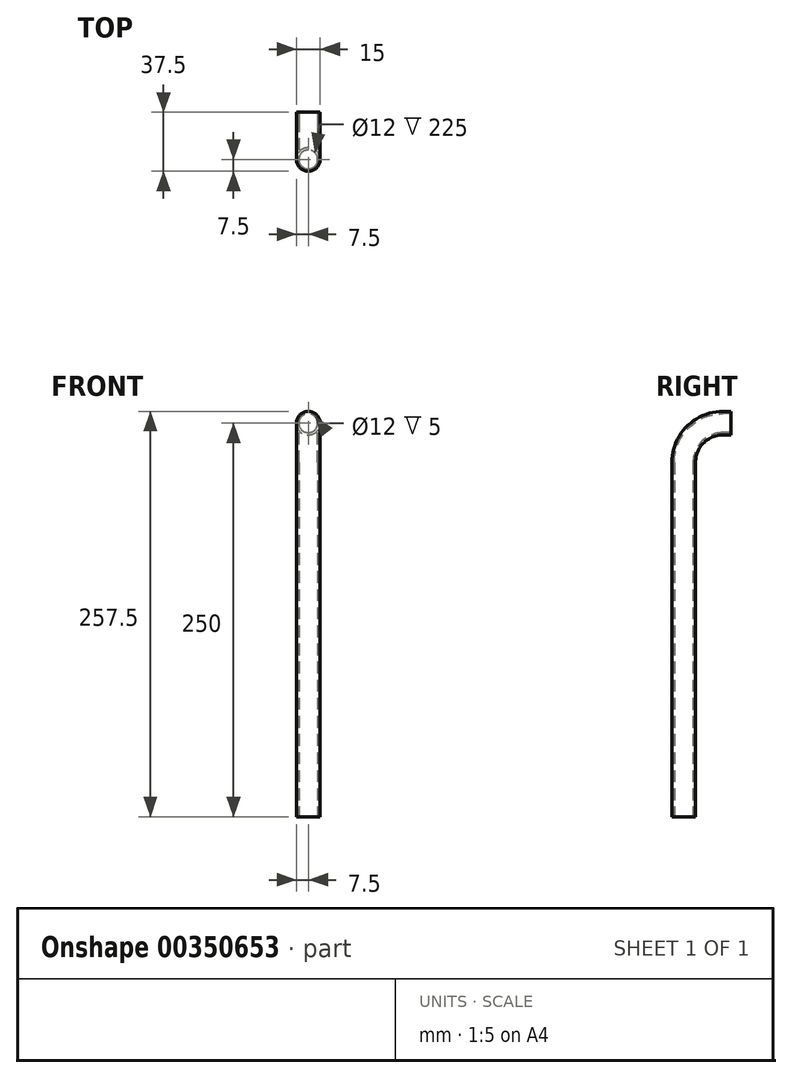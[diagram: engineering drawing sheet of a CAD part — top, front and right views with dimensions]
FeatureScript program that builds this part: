
annotation { "Feature Type Name" : "Feature", "Feature Type Description" : "" }
export const myFeature = defineFeature(function(context is Context, id is Id, definition is map)
    precondition{}
    {
        {
            var Q0;
            Q0=qCreatedBy(makeId("Right.planeOp"),FACE);
            var sketch = newSketch(context, id + "F0", { "sketchPlane" : qUnion([Q0])});
            skLineSegment(sketch, "E0", {"start": v(0, 0) * mm, "end": v(-5, 0) * mm});
            skLineSegment(sketch, "E1", {"start": v(-30, -25) * mm, "end": v(-30, -250) * mm});
            skPoint(sketch, "E2.visualSharp", {"position": v(-30, 0) * mm});
            skArc(sketch, "E2.filletArc", {"start": v(-5, 0) * mm, "mid": v(-22.68, -7.32) * mm, "end": v(-30, -25) * mm});
            skSolve(sketch);
        }
        {
            var Q0;
            Q0=qCreatedBy(makeId("Front.planeOp"),FACE);
            var sketch = newSketch(context, id + "F1", { "sketchPlane" : qUnion([Q0])});
            skCircle(sketch, "E3", {"center": v(0, 0) * mm, "radius": 7.5 * mm});
            skCircle(sketch, "E4", {"center": v(0, 0) * mm, "radius": 6 * mm});
            skSolve(sketch);
        }
        {
            var Q0;
            Q0=makeQuery(id+"F1.imprint","IMPRINT",FACE,{"disambiguationData":[TD([[makeQuery(id+"F1.imprint","IMPRINT",EDGE,{"derivedFrom":sQuery(id+"F1.wireOp",EDGE,"E3")}),1.0]])]});
            var Q1;
            Q1=sQuery(id+"F0.wireOp",EDGE,"E0");
            var Q2;
            Q2=sQuery(id+"F0.wireOp",EDGE,"E2.filletArc");
            var Q3;
            Q3=sQuery(id+"F0.wireOp",EDGE,"E1");
            sweep(context, id + "F2", {"profiles" : qUnion([Q0]), "path" : qUnion([Q1, Q2, Q3])});
        }
    });
